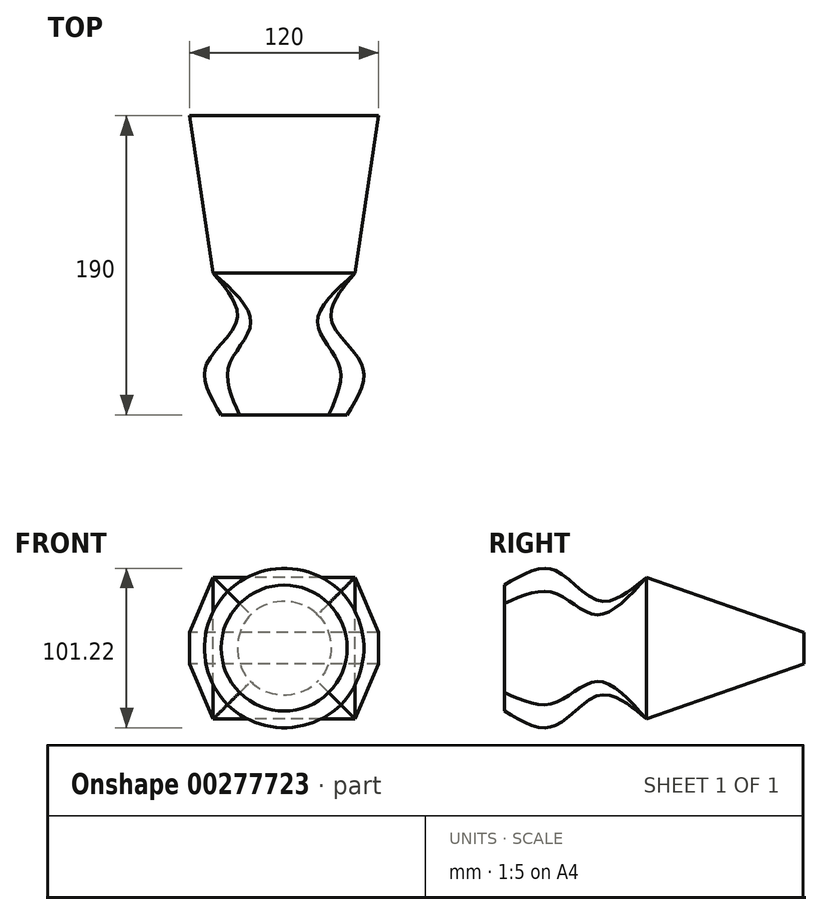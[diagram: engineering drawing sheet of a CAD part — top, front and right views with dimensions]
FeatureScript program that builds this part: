
annotation { "Feature Type Name" : "Feature", "Feature Type Description" : "" }
export const myFeature = defineFeature(function(context is Context, id is Id, definition is map)
    precondition{}
    {
        {
            var Q0;
            Q0=qCreatedBy(makeId("Front.planeOp"),FACE);
            cPlane(context, id + "F0", {"entities" : qUnion([Q0]), "cplaneType" : CPlaneType.OFFSET, "offset" : 30 * mm, "oppositeDirection" : true, "width" : 150 * mm, "height" : 150 * mm});
        }
        {
            var Q0;
            Q0=qCreatedBy(id+"F0.planeOp",FACE);
            cPlane(context, id + "F1", {"entities" : qUnion([Q0]), "cplaneType" : CPlaneType.OFFSET, "offset" : 30 * mm, "oppositeDirection" : true, "width" : 150 * mm, "height" : 150 * mm});
        }
        {
            var Q0;
            Q0=qCreatedBy(id+"F1.planeOp",FACE);
            cPlane(context, id + "F2", {"entities" : qUnion([Q0]), "cplaneType" : CPlaneType.OFFSET, "offset" : 30 * mm, "oppositeDirection" : true, "width" : 150 * mm, "height" : 150 * mm});
        }
        {
            var Q0;
            Q0=qCreatedBy(id+"F2.planeOp",FACE);
            cPlane(context, id + "F3", {"entities" : qUnion([Q0]), "cplaneType" : CPlaneType.OFFSET, "offset" : 100 * mm, "oppositeDirection" : true, "width" : 150 * mm, "height" : 150 * mm});
        }
        {
            var Q0;
            Q0=qCreatedBy(makeId("Front.planeOp"),FACE);
            var sketch = newSketch(context, id + "F4", { "sketchPlane" : qUnion([Q0])});
            skCircle(sketch, "E0", {"center": v(0, 0) * mm, "radius": 40 * mm});
            skSolve(sketch);
        }
        {
            var Q0;
            Q0=qCreatedBy(id+"F0.planeOp",FACE);
            var sketch = newSketch(context, id + "F5", { "sketchPlane" : qUnion([Q0])});
            skCircle(sketch, "E1", {"center": v(0, 0) * mm, "radius": 50 * mm});
            skSolve(sketch);
        }
        {
            var Q0;
            Q0=qCreatedBy(id+"F1.planeOp",FACE);
            var sketch = newSketch(context, id + "F6", { "sketchPlane" : qUnion([Q0])});
            skCircle(sketch, "E2", {"center": v(0, 0) * mm, "radius": 30 * mm});
            skSolve(sketch);
        }
        {
            var Q0;
            Q0=qCreatedBy(id+"F2.planeOp",FACE);
            var sketch = newSketch(context, id + "F7", { "sketchPlane" : qUnion([Q0])});
            skLineSegment(sketch, "E3.bottom", {"start": v(45, -45) * mm, "end": v(-45, -45) * mm});
            skLineSegment(sketch, "E3.top", {"start": v(45, 45) * mm, "end": v(-45, 45) * mm});
            skLineSegment(sketch, "E3.left", {"start": v(45, -45) * mm, "end": v(45, 45) * mm});
            skLineSegment(sketch, "E3.right", {"start": v(-45, -45) * mm, "end": v(-45, 45) * mm});
            skPoint(sketch, "E3.middle", {"position": v(0, 0) * mm});
            skSolve(sketch);
        }
        {
            var Q0;
            Q0=qCreatedBy(id+"F3.planeOp",FACE);
            var sketch = newSketch(context, id + "F8", { "sketchPlane" : qUnion([Q0])});
            skLineSegment(sketch, "E4.bottom", {"start": v(60, -10) * mm, "end": v(-60, -10) * mm});
            skLineSegment(sketch, "E4.top", {"start": v(60, 10) * mm, "end": v(-60, 10) * mm});
            skLineSegment(sketch, "E4.left", {"start": v(60, -10) * mm, "end": v(60, 10) * mm});
            skLineSegment(sketch, "E4.right", {"start": v(-60, -10) * mm, "end": v(-60, 10) * mm});
            skPoint(sketch, "E4.middle", {"position": v(0, 0) * mm});
            skSolve(sketch);
        }
        {
            var Q0;
            Q0 = qSketchRegion(id + "F4", true);
            var Q1;
            Q1 = qSketchRegion(id + "F5", true);
            var Q2;
            Q2 = qSketchRegion(id + "F6", true);
            var Q3;
            Q3 = qSketchRegion(id + "F7", true);
            loft(context, id + "F9", {"sheetProfilesArray" : [{ "sheetProfileEntities" : qUnion([Q0]) }, { "sheetProfileEntities" : qUnion([Q1]) }, { "sheetProfileEntities" : qUnion([Q2]) }, { "sheetProfileEntities" : qUnion([Q3]) }]});
        }
        {
            var Q1;
            Q1 = qSketchRegion(id + "F7", true);
            var Q2;
            Q2 = qSketchRegion(id + "F8", true);
            loft(context, id + "F10", {"operationType" : NewBodyOperationType.ADD, "sheetProfilesArray" : [{ "sheetProfileEntities" : qUnion([Q1]) }, { "sheetProfileEntities" : qUnion([Q2]) }]});
        }
    });
